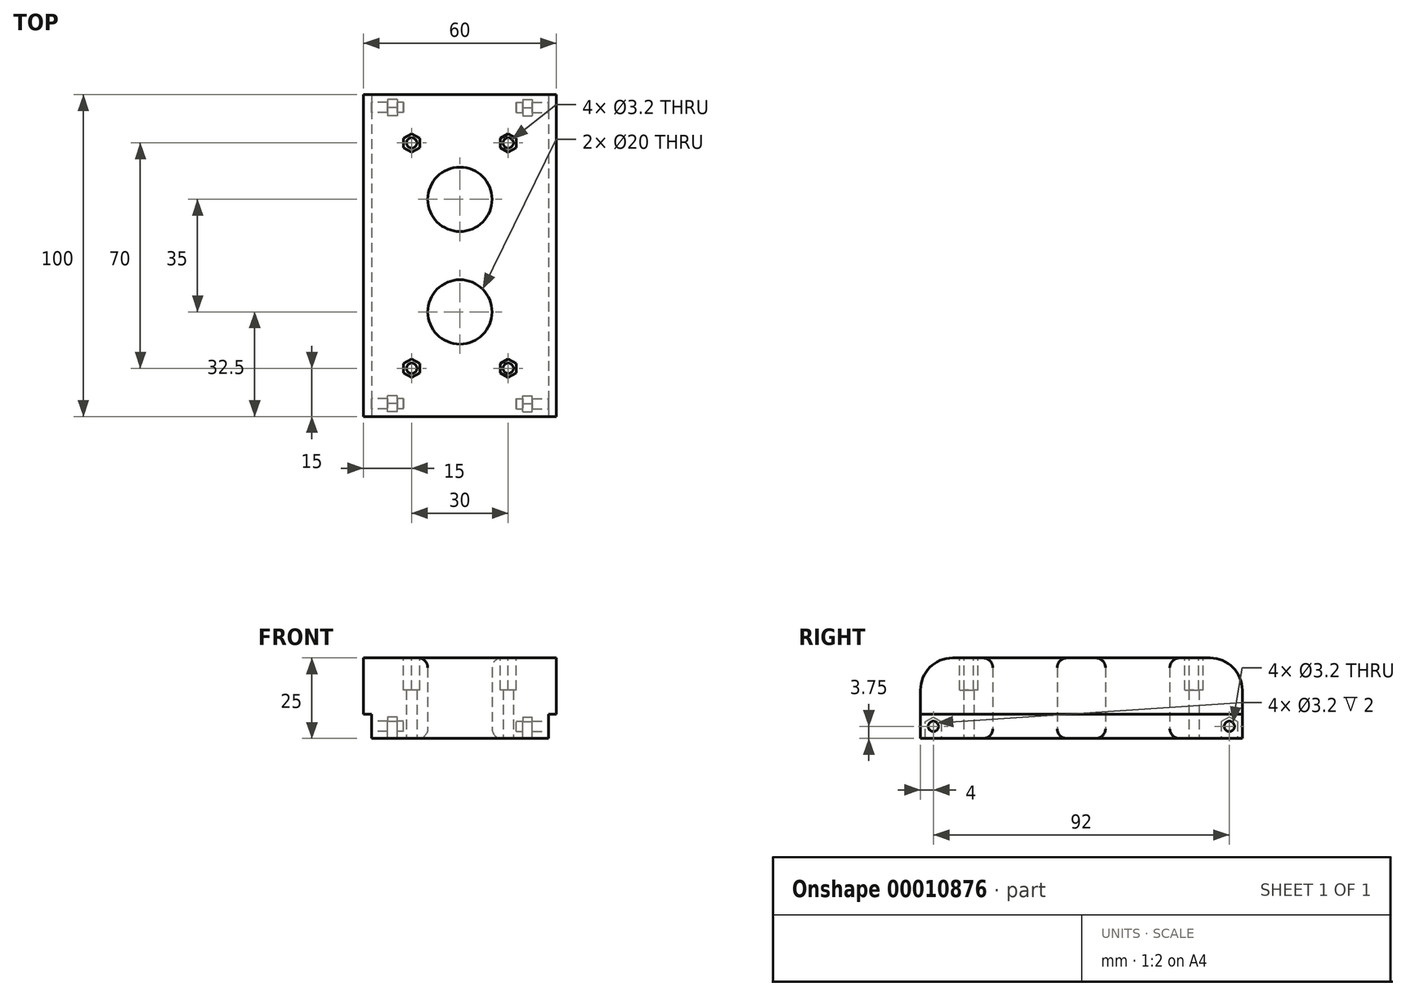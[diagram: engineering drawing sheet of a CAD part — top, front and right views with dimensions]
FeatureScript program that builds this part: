
annotation { "Feature Type Name" : "Feature", "Feature Type Description" : "" }
export const myFeature = defineFeature(function(context is Context, id is Id, definition is map)
    precondition{}
    {
        {
            var Q0;
            Q0=qCreatedBy(makeId("Top.planeOp"),FACE);
            var sketch = newSketch(context, id + "F0", { "sketchPlane" : qUnion([Q0])});
            skLineSegment(sketch, "E0.bottom", {"start": v(0, 50) * mm, "end": v(30, 50) * mm});
            skLineSegment(sketch, "E0.top", {"start": v(0, -50) * mm, "end": v(30, -50) * mm});
            skLineSegment(sketch, "E0.left", {"start": v(-30, 50) * mm, "end": v(-30, -50) * mm, "construction": true});
            skLineSegment(sketch, "E0.right", {"start": v(30, 50) * mm, "end": v(30, -50) * mm});
            skLineSegment(sketch, "E1", {"start": v(-30, 50) * mm, "end": v(30, -50) * mm, "construction": true});
            skLineSegment(sketch, "E2", {"start": v(0, -50) * mm, "end": v(0, -27.5) * mm});
            skLineSegment(sketch, "E3", {"start": v(-30, -50) * mm, "end": v(0, -50) * mm, "construction": true});
            skLineSegment(sketch, "E4", {"start": v(-30, 50) * mm, "end": v(0, 50) * mm, "construction": true});
            skLineSegment(sketch, "E5.trimOffspring", {"start": v(0, 27.5) * mm, "end": v(0, 50) * mm});
            skArc(sketch, "E6", {"start": v(0, 7.5) * mm, "mid": v(10, 17.5) * mm, "end": v(0, 27.5) * mm});
            skArc(sketch, "E7", {"start": v(0, -27.5) * mm, "mid": v(10, -17.5) * mm, "end": v(0, -7.5) * mm});
            skLineSegment(sketch, "E8", {"start": v(0, -7.5) * mm, "end": v(0, 7.5) * mm});
            skSolve(sketch);
        }
        {
            var Q0;
            Q0 = qSketchRegion(id + "F0", true);
            extrude(context, id + "F1", {"entities" : qUnion([Q0]), "depth" : 25 * mm});
        }
        {
            var Q0;
            Q0=makeQuery(id+"F1.opExtrude","CAP_EDGE",EDGE,{"disambiguationData":[OSD([sQuery(id+"F0.wireOp",EDGE,"e43dd0de-8b86-428c-9d10-86988c666313")])],"isStart":false});
            var Q1;
            Q1=makeQuery(id+"F1.opExtrude","CAP_EDGE",EDGE,{"disambiguationData":[OSD([sQuery(id+"F0.wireOp",EDGE,"e43dd0de-8b86-428c-9d10-86988c666313")])],"isStart":true});
            var Q2;
            Q2=makeQuery(id+"F1.opExtrude","CAP_EDGE",EDGE,{"disambiguationData":[OSD([sQuery(id+"F0.wireOp",EDGE,"E6")])],"isStart":false});
            var Q3;
            Q3=makeQuery(id+"F1.opExtrude","CAP_EDGE",EDGE,{"disambiguationData":[OSD([sQuery(id+"F0.wireOp",EDGE,"E7")])],"isStart":false});
            var Q4;
            Q4=makeQuery(id+"F1.opExtrude","CAP_EDGE",EDGE,{"disambiguationData":[OSD([sQuery(id+"F0.wireOp",EDGE,"E6")])],"isStart":true});
            var Q5;
            Q5=makeQuery(id+"F1.opExtrude","CAP_EDGE",EDGE,{"disambiguationData":[OSD([sQuery(id+"F0.wireOp",EDGE,"E7")])],"isStart":true});
            fillet(context, id + "F2", {"entities" : qUnion([Q0, Q1, Q2, Q3, Q4, Q5]), "radius" : 3 * mm, "tangentPropagation" : true, "allowEdgeOverflow" : false});
        }
        {
            var Q0;
            Q0=makeQuery(id+"F1.opExtrude","CAP_EDGE",EDGE,{"disambiguationData":[OSD([sQuery(id+"F0.wireOp",EDGE,"E0.top")])],"isStart":false});
            var Q1;
            Q1=makeQuery(id+"F1.opExtrude","CAP_EDGE",EDGE,{"disambiguationData":[OSD([sQuery(id+"F0.wireOp",EDGE,"E0.bottom")])],"isStart":false});
            fillet(context, id + "F3", {"entities" : qUnion([Q0, Q1]), "radius" : 10 * mm, "tangentPropagation" : true, "allowEdgeOverflow" : false});
        }
        {
            var Q0;
            Q0=makeQuery(id+"F1.opExtrude","SWEPT_FACE",FACE,{"disambiguationData":[OSD([sQuery(id+"F0.wireOp",EDGE,"E0.top")])]});
            var sketch = newSketch(context, id + "F4", { "sketchPlane" : qUnion([Q0])});
            skLineSegment(sketch, "E9.bottom", {"start": v(30, 0) * mm, "end": v(27.5, 0) * mm});
            skLineSegment(sketch, "E9.top", {"start": v(30, 7.5) * mm, "end": v(27.5, 7.5) * mm});
            skLineSegment(sketch, "E9.left", {"start": v(30, 0) * mm, "end": v(30, 7.5) * mm});
            skLineSegment(sketch, "E9.right", {"start": v(27.5, 0) * mm, "end": v(27.5, 7.5) * mm});
            skSolve(sketch);
        }
        {
            var Q0;
            Q0 = qSketchRegion(id + "F4", true);
            extrude(context, id + "F5", {"entities" : qUnion([Q0]), "operationType" : NewBodyOperationType.REMOVE, "endBound" : BoundingType.THROUGH_ALL, "oppositeDirection" : true, "depth" : 25 * mm});
        }
        {
            var Q0;
            Q0=makeQuery(id+"F5.boolean.opBoolean","COPY",FACE,{"derivedFrom":makeQuery(id+"F5.opExtrude","SWEPT_FACE",FACE,{"disambiguationData":[OSD([sQuery(id+"F4.wireOp",EDGE,"E9.right")])]})});
            var sketch = newSketch(context, id + "F6", { "sketchPlane" : qUnion([Q0])});
            skLineSegment(sketch, "E10", {"start": v(-46, 3.75) * mm, "end": v(0, 3.75) * mm, "construction": true});
            skLineSegment(sketch, "E11", {"start": v(0, 3.75) * mm, "end": v(46, 3.75) * mm, "construction": true});
            skCircle(sketch, "E12", {"center": v(-46, 3.75) * mm, "radius": 1.6 * mm});
            skCircle(sketch, "E13", {"center": v(46, 3.75) * mm, "radius": 1.6 * mm});
            skLineSegment(sketch, "E14", {"start": v(0, 0) * mm, "end": v(0, 3.75) * mm, "construction": true});
            skSolve(sketch);
        }
        {
            var Q0;
            Q0 = qSketchRegion(id + "F6", true);
            extrude(context, id + "F7", {"entities" : qUnion([Q0]), "operationType" : NewBodyOperationType.REMOVE, "oppositeDirection" : true, "depth" : 10 * mm});
        }
        {
            var Q0;
            Q0=makeQuery(id+"F5.boolean.opBoolean","COPY",FACE,{"derivedFrom":makeQuery(id+"F5.opExtrude","SWEPT_FACE",FACE,{"disambiguationData":[OSD([sQuery(id+"F4.wireOp",EDGE,"E9.right")])]})});
            cPlane(context, id + "F8", {"entities" : qUnion([Q0]), "cplaneType" : CPlaneType.OFFSET, "offset" : 5 * mm, "oppositeDirection" : true, "width" : 150 * mm, "height" : 150 * mm});
        }
        {
            var Q0;
            Q0=qCreatedBy(id+"F8.planeOp",FACE);
            var sketch = newSketch(context, id + "F9", { "sketchPlane" : qUnion([Q0])});
            skCircle(sketch, "E15.cCircle", {"center": v(-46, 3.75) * mm, "radius": 2.5 * mm, "construction": true});
            skLineSegment(sketch, "E15.0", {"start": v(-46, 0.86) * mm, "end": v(-48.5, 2.3) * mm, "construction": true});
            skLineSegment(sketch, "E15.1", {"start": v(-48.5, 2.3) * mm, "end": v(-48.5, 5.2) * mm});
            skLineSegment(sketch, "E15.2", {"start": v(-48.5, 5.2) * mm, "end": v(-46, 6.64) * mm});
            skLineSegment(sketch, "E15.3", {"start": v(-46, 6.64) * mm, "end": v(-43.5, 5.2) * mm});
            skLineSegment(sketch, "E15.4", {"start": v(-43.5, 5.2) * mm, "end": v(-43.5, 2.3) * mm});
            skLineSegment(sketch, "E15.5", {"start": v(-43.5, 2.3) * mm, "end": v(-46, 0.86) * mm, "construction": true});
            skPoint(sketch, "E15.0.midPoint", {"position": v(-47.25, 1.58) * mm});
            skLineSegment(sketch, "E16.bottom", {"start": v(-48.5, 2.3) * mm, "end": v(-43.5, 2.3) * mm, "construction": true});
            skLineSegment(sketch, "E16.top", {"start": v(-48.5, 0) * mm, "end": v(-43.5, 0) * mm});
            skLineSegment(sketch, "E16.left", {"start": v(-48.5, 2.3) * mm, "end": v(-48.5, 0) * mm});
            skLineSegment(sketch, "E16.right", {"start": v(-43.5, 2.3) * mm, "end": v(-43.5, 0) * mm});
            skLineSegment(sketch, "E17", {"start": v(-46, 3.75) * mm, "end": v(0, 3.75) * mm, "construction": true});
            skLineSegment(sketch, "E18.11.MirrorCS", {"start": v(0, 3.75) * mm, "end": v(-46, 3.75) * mm, "construction": true});
            skLineSegment(sketch, "E19", {"start": v(0, 3.75) * mm, "end": v(47.46, 3.75) * mm, "construction": true});
            skLineSegment(sketch, "E20", {"start": v(0, 3.75) * mm, "end": v(0, 11.08) * mm, "construction": true});
            skLineSegment(sketch, "E21.0.MirrorCS", {"start": v(48.5, 2.3) * mm, "end": v(48.5, 0) * mm});
            skLineSegment(sketch, "E21.1.MirrorCS", {"start": v(0, 3.75) * mm, "end": v(46, 3.75) * mm, "construction": true});
            skLineSegment(sketch, "E21.2.MirrorCS", {"start": v(43.5, 2.3) * mm, "end": v(43.5, 0) * mm});
            skLineSegment(sketch, "E21.3.MirrorCS", {"start": v(46, 0.86) * mm, "end": v(48.5, 2.3) * mm, "construction": true});
            skLineSegment(sketch, "E21.4.MirrorCS", {"start": v(43.5, 2.3) * mm, "end": v(46, 0.86) * mm, "construction": true});
            skLineSegment(sketch, "E21.5.MirrorCS", {"start": v(48.5, 5.2) * mm, "end": v(46, 6.64) * mm});
            skPoint(sketch, "E21.6.MirrorP", {"position": v(47.25, 1.58) * mm});
            skCircle(sketch, "E21.7.MirrorC", {"center": v(46, 3.75) * mm, "radius": 2.5 * mm, "construction": true});
            skLineSegment(sketch, "E21.8.MirrorCS", {"start": v(46, 6.64) * mm, "end": v(43.5, 5.2) * mm});
            skLineSegment(sketch, "E21.9.MirrorCS", {"start": v(48.5, 0) * mm, "end": v(43.5, 0) * mm});
            skLineSegment(sketch, "E21.10.MirrorCS", {"start": v(46, 3.75) * mm, "end": v(0, 3.75) * mm, "construction": true});
            skLineSegment(sketch, "E21.11.MirrorCS", {"start": v(43.5, 5.2) * mm, "end": v(43.5, 2.3) * mm});
            skLineSegment(sketch, "E21.12.MirrorCS", {"start": v(48.5, 2.3) * mm, "end": v(43.5, 2.3) * mm, "construction": true});
            skLineSegment(sketch, "E21.13.MirrorCS", {"start": v(48.5, 2.3) * mm, "end": v(48.5, 5.2) * mm});
            skSolve(sketch);
        }
        {
            var Q0;
            Q0 = qSketchRegion(id + "F9", true);
            extrude(context, id + "F10", {"entities" : qUnion([Q0]), "operationType" : NewBodyOperationType.REMOVE, "oppositeDirection" : true, "depth" : 3 * mm});
        }
        {
            var Q0;
            Q0=makeQuery(id+"F1.opExtrude","SWEPT_BODY",BODY,{"disambiguationData":[OSD([sQuery(id+"F0.wireOp",EDGE,"E0.bottom"),sQuery(id+"F0.wireOp",EDGE,"E0.top"),sQuery(id+"F0.wireOp",EDGE,"E0.right"),sQuery(id+"F0.wireOp",EDGE,"e43dd0de-8b86-428c-9d10-86988c666313"),sQuery(id+"F0.wireOp",EDGE,"E2"),sQuery(id+"F0.wireOp",EDGE,"E5.trimOffspring")])]});
            var Q1;
            Q1=qCreatedBy(makeId("Right.planeOp"),FACE);
            mirror(context, id + "F11", {"operationType" : NewBodyOperationType.ADD, "entities" : qUnion([Q0]), "mirrorPlane" : qUnion([Q1])});
        }
        {
            var Q0;
            {var subQ0=makeQuery(id+"F1.opExtrude","CAP_FACE",FACE,{"disambiguationData":[OSD([sQuery(id+"F0.wireOp",EDGE,"E0.bottom"),sQuery(id+"F0.wireOp",EDGE,"E0.top"),sQuery(id+"F0.wireOp",EDGE,"E0.right"),sQuery(id+"F0.wireOp",EDGE,"E2"),sQuery(id+"F0.wireOp",EDGE,"E5.trimOffspring"),sQuery(id+"F0.wireOp",EDGE,"E6"),sQuery(id+"F0.wireOp",EDGE,"E7"),sQuery(id+"F0.wireOp",EDGE,"E8")])],"isStart":true});Q0=makeQuery(id+"F11.boolean.opBoolean","MERGE",FACE,{"derivedFrom":[subQ0,makeQuery(id+"F11.opPattern","COPY",FACE,{"derivedFrom":subQ0,"instanceName":"1"})]});}
            var sketch = newSketch(context, id + "F12", { "sketchPlane" : qUnion([Q0])});
            skLineSegment(sketch, "E22.bottom", {"start": v(15, 35) * mm, "end": v(-15, 35) * mm, "construction": true});
            skLineSegment(sketch, "E22.top", {"start": v(15, 0) * mm, "end": v(-15, 0) * mm, "construction": true});
            skLineSegment(sketch, "E22.left", {"start": v(15, 35) * mm, "end": v(15, 0) * mm, "construction": true});
            skLineSegment(sketch, "E22.right", {"start": v(-15, 35) * mm, "end": v(-15, 0) * mm, "construction": true});
            skLineSegment(sketch, "E23.top", {"start": v(15, -35) * mm, "end": v(-15, -35) * mm, "construction": true});
            skLineSegment(sketch, "E23.left", {"start": v(15, 0) * mm, "end": v(15, -35) * mm, "construction": true});
            skLineSegment(sketch, "E23.right", {"start": v(-15, 0) * mm, "end": v(-15, -35) * mm, "construction": true});
            skCircle(sketch, "E24", {"center": v(15, 35) * mm, "radius": 1.6 * mm});
            skCircle(sketch, "E25", {"center": v(-15, 35) * mm, "radius": 1.6 * mm});
            skCircle(sketch, "E26", {"center": v(15, -35) * mm, "radius": 1.6 * mm});
            skCircle(sketch, "E27", {"center": v(-15, -35) * mm, "radius": 1.6 * mm});
            skPoint(sketch, "E28", {"position": v(0, 17.5) * mm});
            skLineSegment(sketch, "E29", {"start": v(-15, 35) * mm, "end": v(15, 0) * mm, "construction": true});
            skLineSegment(sketch, "E30", {"start": v(-15, 0) * mm, "end": v(15, -35) * mm, "construction": true});
            skPoint(sketch, "E31", {"position": v(0, -17.5) * mm});
            skSolve(sketch);
        }
        {
            var Q0;
            Q0 = qSketchRegion(id + "F12", true);
            extrude(context, id + "F13", {"entities" : qUnion([Q0]), "operationType" : NewBodyOperationType.REMOVE, "oppositeDirection" : true, "depth" : 20 * mm});
        }
        {
            var Q0;
            {var subQ0=makeQuery(id+"F1.opExtrude","CAP_FACE",FACE,{"disambiguationData":[OSD([sQuery(id+"F0.wireOp",EDGE,"E0.bottom"),sQuery(id+"F0.wireOp",EDGE,"E0.top"),sQuery(id+"F0.wireOp",EDGE,"E0.right"),sQuery(id+"F0.wireOp",EDGE,"E2"),sQuery(id+"F0.wireOp",EDGE,"E5.trimOffspring"),sQuery(id+"F0.wireOp",EDGE,"E6"),sQuery(id+"F0.wireOp",EDGE,"E7"),sQuery(id+"F0.wireOp",EDGE,"E8")])],"isStart":false});Q0=makeQuery(id+"F11.boolean.opBoolean","MERGE",FACE,{"derivedFrom":[subQ0,makeQuery(id+"F11.opPattern","COPY",FACE,{"derivedFrom":subQ0,"instanceName":"1"})]});}
            var sketch = newSketch(context, id + "F14", { "sketchPlane" : qUnion([Q0])});
            skCircle(sketch, "E32.cCircle", {"center": v(15, 35) * mm, "radius": 2.5 * mm, "construction": true});
            skLineSegment(sketch, "E32.0", {"start": v(12.5, 33.56) * mm, "end": v(12.5, 36.44) * mm});
            skLineSegment(sketch, "E32.1", {"start": v(12.5, 36.44) * mm, "end": v(15, 37.89) * mm});
            skLineSegment(sketch, "E32.2", {"start": v(15, 37.89) * mm, "end": v(17.5, 36.44) * mm});
            skLineSegment(sketch, "E32.3", {"start": v(17.5, 36.44) * mm, "end": v(17.5, 33.56) * mm});
            skLineSegment(sketch, "E32.4", {"start": v(17.5, 33.56) * mm, "end": v(15, 32.11) * mm});
            skLineSegment(sketch, "E32.5", {"start": v(15, 32.11) * mm, "end": v(12.5, 33.56) * mm});
            skPoint(sketch, "E32.0.midPoint", {"position": v(12.5, 35) * mm});
            skCircle(sketch, "E33.cCircle", {"center": v(-15, 35) * mm, "radius": 2.5 * mm, "construction": true});
            skLineSegment(sketch, "E33.0", {"start": v(-17.5, 33.56) * mm, "end": v(-17.5, 36.44) * mm});
            skLineSegment(sketch, "E33.1", {"start": v(-17.5, 36.44) * mm, "end": v(-15, 37.89) * mm});
            skLineSegment(sketch, "E33.2", {"start": v(-15, 37.89) * mm, "end": v(-12.5, 36.44) * mm});
            skLineSegment(sketch, "E33.3", {"start": v(-12.5, 36.44) * mm, "end": v(-12.5, 33.56) * mm});
            skLineSegment(sketch, "E33.4", {"start": v(-12.5, 33.56) * mm, "end": v(-15, 32.11) * mm});
            skLineSegment(sketch, "E33.5", {"start": v(-15, 32.11) * mm, "end": v(-17.5, 33.56) * mm});
            skPoint(sketch, "E33.0.midPoint", {"position": v(-17.5, 35) * mm});
            skCircle(sketch, "E34.cCircle", {"center": v(-15, -35) * mm, "radius": 2.5 * mm, "construction": true});
            skLineSegment(sketch, "E34.0", {"start": v(-17.5, -36.44) * mm, "end": v(-17.5, -33.56) * mm});
            skLineSegment(sketch, "E34.1", {"start": v(-17.5, -33.56) * mm, "end": v(-15, -32.11) * mm});
            skLineSegment(sketch, "E34.2", {"start": v(-15, -32.11) * mm, "end": v(-12.5, -33.56) * mm});
            skLineSegment(sketch, "E34.3", {"start": v(-12.5, -33.56) * mm, "end": v(-12.5, -36.44) * mm});
            skLineSegment(sketch, "E34.4", {"start": v(-12.5, -36.44) * mm, "end": v(-15, -37.89) * mm});
            skLineSegment(sketch, "E34.5", {"start": v(-15, -37.89) * mm, "end": v(-17.5, -36.44) * mm});
            skPoint(sketch, "E34.0.midPoint", {"position": v(-17.5, -35) * mm});
            skCircle(sketch, "E35.cCircle", {"center": v(15, -35) * mm, "radius": 2.5 * mm, "construction": true});
            skLineSegment(sketch, "E35.0", {"start": v(12.5, -36.44) * mm, "end": v(12.5, -33.56) * mm});
            skLineSegment(sketch, "E35.1", {"start": v(12.5, -33.56) * mm, "end": v(15, -32.11) * mm});
            skLineSegment(sketch, "E35.2", {"start": v(15, -32.11) * mm, "end": v(17.5, -33.56) * mm});
            skLineSegment(sketch, "E35.3", {"start": v(17.5, -33.56) * mm, "end": v(17.5, -36.44) * mm});
            skLineSegment(sketch, "E35.4", {"start": v(17.5, -36.44) * mm, "end": v(15, -37.89) * mm});
            skLineSegment(sketch, "E35.5", {"start": v(15, -37.89) * mm, "end": v(12.5, -36.44) * mm});
            skPoint(sketch, "E35.0.midPoint", {"position": v(12.5, -35) * mm});
            skSolve(sketch);
        }
        {
            var Q0;
            Q0 = qSketchRegion(id + "F14", true);
            extrude(context, id + "F15", {"entities" : qUnion([Q0]), "operationType" : NewBodyOperationType.REMOVE, "oppositeDirection" : true, "depth" : 10 * mm});
        }
    });
